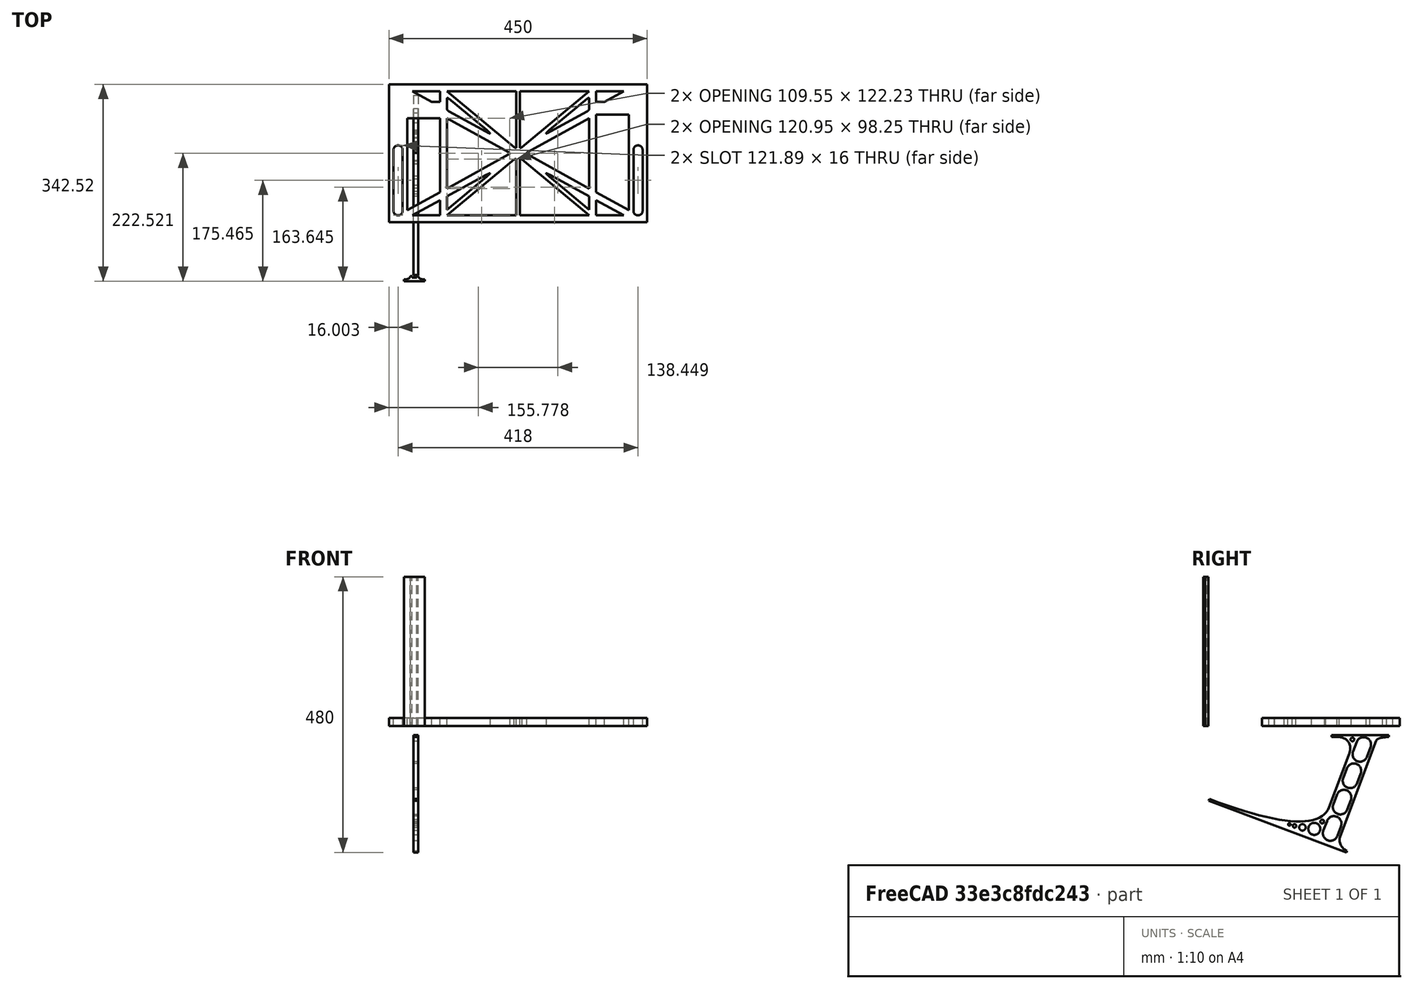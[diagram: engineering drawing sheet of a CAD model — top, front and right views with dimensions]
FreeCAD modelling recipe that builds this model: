
FCSTD DOCUMENT  (FreeCAD 0.19R0.19.2)
Label: laptopStand073
License: All rights reserved
LicenseURL: http://en.wikipedia.org/wiki/All_rights_reserved
objects: Sketcher::SketchObject×3, Part::Extrusion×3
note: 6 computed .brp shape members not serialized (recipe doc carries the construction recipe); baked Part::Feature solids carry a one-line shape summary decoded from their .brp

FEATURE [Sketcher::SketchObject] Sketch
  FullyConstrained = true
  sketch-geometry (148):
    g0: LineSegment StartX=-10.9272 StartY=-82.7794 StartZ=0 EndX=46.0728 EndY=-51.4823 EndZ=0
    g1: LineSegment StartX=366.073 StartY=-91.7794 StartZ=0 EndX=318.073 EndY=-65.424 EndZ=0
    g2: LineSegment StartX=-10.9272 StartY=77.3346 StartZ=0 EndX=-10.9272 EndY=-82.7794 EndZ=0
    g3: LineSegment StartX=375.073 StartY=-82.7794 StartZ=0 EndX=375.073 EndY=83.9235 EndZ=0
    g4: LineSegment StartX=-1.92719 StartY=-91.7794 StartZ=0 EndX=46.0728 EndY=-91.7794 EndZ=0
    g5: LineSegment StartX=318.073 StartY=124.221 StartZ=0 EndX=366.073 EndY=124.221 EndZ=0
    g6: LineSegment StartX=306.073 StartY=124.221 StartZ=0 EndX=189.124 EndY=27.0628 EndZ=0
    g7: LineSegment StartX=58.0728 StartY=-91.7794 StartZ=0 EndX=175.022 EndY=5.37834 EndZ=0
    g8: LineSegment StartX=58.0728 StartY=-81.8102 StartZ=0 EndX=58.0728 EndY=-58.8351 EndZ=0
    g9: LineSegment StartX=175.022 StartY=27.0628 StartZ=0 EndX=58.0728 EndY=124.221 EndZ=0
    g10: LineSegment StartX=189.124 StartY=5.37834 StartZ=0 EndX=306.073 EndY=-91.7794 EndZ=0
    g11: LineSegment StartX=306.073 StartY=77.3346 StartZ=0 EndX=306.073 EndY=-44.8935 EndZ=0
    g12: LineSegment StartX=318.073 StartY=83.9235 StartZ=0 EndX=318.073 EndY=-51.4823 EndZ=0
    g13: LineSegment StartX=306.073 StartY=-58.8351 StartZ=0 EndX=306.073 EndY=-81.8102 EndZ=0
    g14: LineSegment StartX=318.073 StartY=-51.4823 StartZ=0 EndX=375.073 EndY=-82.7794 EndZ=0
    g15: LineSegment StartX=318.073 StartY=-65.424 StartZ=0 EndX=318.073 EndY=-91.7794 EndZ=0
    g16: LineSegment StartX=318.073 StartY=-91.7794 StartZ=0 EndX=366.073 EndY=-91.7794 EndZ=0
    g17: LineSegment StartX=58.0728 StartY=-44.8935 StartZ=0 EndX=58.0728 EndY=77.3346 EndZ=0
    g18: LineSegment StartX=46.0728 StartY=-65.424 StartZ=0 EndX=-1.92719 EndY=-91.7794 EndZ=0
    g19: LineSegment StartX=46.0728 StartY=-65.424 StartZ=0 EndX=46.0728 EndY=-91.7794 EndZ=0
    g20: LineSegment StartX=46.0728 StartY=77.3346 StartZ=0 EndX=46.0728 EndY=-51.4823 EndZ=0
    g21: LineSegment StartX=-42.9272 StartY=136.221 StartZ=0 EndX=-42.9272 EndY=-103.779 EndZ=0
    g22: LineSegment StartX=407.073 StartY=136.221 StartZ=0 EndX=407.073 EndY=-103.779 EndZ=0
    g23: LineSegment StartX=179.022 StartY=27.0628 StartZ=0 EndX=179.022 EndY=124.221 EndZ=0
    g24: LineSegment StartX=185.124 StartY=27.0628 StartZ=0 EndX=185.124 EndY=124.221 EndZ=0
    g25: ArcOfCircle CenterX=-26.9272 CenterY=22.1087 CenterZ=0 NormalX=0 NormalY=0 NormalZ=1 AngleXU=0 Radius=8 StartAngle=1e-16 EndAngle=3.14159
    g26: ArcOfCircle CenterX=-26.9272 CenterY=-83.7794 CenterZ=0 NormalX=0 NormalY=0 NormalZ=1 AngleXU=0 Radius=8 StartAngle=3.14159 EndAngle=6.28319
    g27: LineSegment StartX=-34.9272 StartY=22.1087 StartZ=0 EndX=-34.9272 EndY=-83.7794 EndZ=0
    g28: LineSegment StartX=-18.9272 StartY=22.1087 StartZ=0 EndX=-18.9272 EndY=-83.7794 EndZ=0
    g29: LineSegment StartX=185.124 StartY=-91.7794 StartZ=0 EndX=306.073 EndY=-91.7794 EndZ=0
    g30: LineSegment StartX=179.022 StartY=-91.7794 StartZ=0 EndX=58.0728 EndY=-91.7794 EndZ=0
    g31: LineSegment StartX=306.073 StartY=124.221 StartZ=0 EndX=185.124 EndY=124.221 EndZ=0
    g32: LineSegment StartX=179.022 StartY=124.221 StartZ=0 EndX=58.0728 EndY=124.221 EndZ=0
    g33: ArcOfCircle CenterX=391.073 CenterY=22.1087 CenterZ=0 NormalX=0 NormalY=0 NormalZ=1 AngleXU=0 Radius=8 StartAngle=-4.4e-15 EndAngle=3.14159
    g34: LineSegment StartX=399.073 StartY=22.1087 StartZ=0 EndX=399.073 EndY=-83.7794 EndZ=0
    g35: LineSegment StartX=383.073 StartY=22.1087 StartZ=0 EndX=383.073 EndY=-83.7794 EndZ=0
    g36: ArcOfCircle CenterX=391.073 CenterY=-83.7794 CenterZ=0 NormalX=0 NormalY=0 NormalZ=1 AngleXU=0 Radius=8 StartAngle=3.14159 EndAngle=6.28319
    g37: Circle CenterX=175.022 CenterY=27.0628 CenterZ=0 NormalX=0 NormalY=0 NormalZ=1 AngleXU=0 Radius=1
    g38: Circle CenterX=179.022 CenterY=24.8665 CenterZ=0 NormalX=0 NormalY=0 NormalZ=1 AngleXU=0 Radius=1
    g39: Circle CenterX=179.022 CenterY=27.0628 CenterZ=0 NormalX=0 NormalY=0 NormalZ=1 AngleXU=0 Radius=1
    g40: BSplineCurve PolesCount=3 KnotsCount=2 Degree=2 IsPeriodic=0
    g41: GeomPoint X=175.022 Y=27.0628 Z=0
    g42: GeomPoint X=179.022 Y=27.0628 Z=0
    g43: Circle CenterX=189.124 CenterY=27.0628 CenterZ=0 NormalX=0 NormalY=0 NormalZ=1 AngleXU=0 Radius=1
    g44: Circle CenterX=185.124 CenterY=24.8665 CenterZ=0 NormalX=0 NormalY=0 NormalZ=1 AngleXU=0 Radius=1
    g45: Circle CenterX=185.124 CenterY=27.0628 CenterZ=0 NormalX=0 NormalY=0 NormalZ=1 AngleXU=0 Radius=1
    g46: BSplineCurve PolesCount=3 KnotsCount=2 Degree=2 IsPeriodic=0
    g47: GeomPoint X=189.124 Y=27.0628 Z=0
    g48: GeomPoint X=185.124 Y=27.0628 Z=0
    g49: Circle CenterX=175.022 CenterY=5.37834 CenterZ=0 NormalX=0 NormalY=0 NormalZ=1 AngleXU=0 Radius=1
    g50: Circle CenterX=179.022 CenterY=7.57463 CenterZ=0 NormalX=0 NormalY=0 NormalZ=1 AngleXU=0 Radius=1
    g51: Circle CenterX=179.022 CenterY=5.34704 CenterZ=0 NormalX=0 NormalY=0 NormalZ=1 AngleXU=0 Radius=1
    g52: BSplineCurve PolesCount=3 KnotsCount=2 Degree=2 IsPeriodic=0
    g53: GeomPoint X=175.022 Y=5.37834 Z=0
    g54: GeomPoint X=179.022 Y=5.34704 Z=0
    g55: Circle CenterX=189.124 CenterY=5.37834 CenterZ=0 NormalX=0 NormalY=0 NormalZ=1 AngleXU=0 Radius=1
    g56: Circle CenterX=185.124 CenterY=7.57463 CenterZ=0 NormalX=0 NormalY=0 NormalZ=1 AngleXU=0 Radius=1
    g57: Circle CenterX=185.124 CenterY=5.34704 CenterZ=0 NormalX=0 NormalY=0 NormalZ=1 AngleXU=0 Radius=1
    g58: BSplineCurve PolesCount=3 KnotsCount=2 Degree=2 IsPeriodic=0
    g59: GeomPoint X=189.124 Y=5.37834 Z=0
    g60: GeomPoint X=185.124 Y=5.34704 Z=0
    g61: LineSegment StartX=179.022 StartY=5.34704 StartZ=0 EndX=179.022 EndY=-91.7794 EndZ=0
    g62: LineSegment StartX=185.124 StartY=-91.7794 StartZ=0 EndX=185.124 EndY=5.34704 EndZ=0
    g63: Circle CenterX=165.871 CenterY=18.1458 CenterZ=0 NormalX=0 NormalY=0 NormalZ=1 AngleXU=0 Radius=1
    g64: Circle CenterX=169.377 CenterY=16.2206 CenterZ=0 NormalX=0 NormalY=0 NormalZ=1 AngleXU=0 Radius=1
    g65: Circle CenterX=165.871 CenterY=14.2954 CenterZ=0 NormalX=0 NormalY=0 NormalZ=1 AngleXU=0 Radius=1
    g66: BSplineCurve PolesCount=3 KnotsCount=2 Degree=2 IsPeriodic=0
    g67: GeomPoint X=165.871 Y=18.1458 Z=0
    g68: GeomPoint X=165.871 Y=14.2954 Z=0
    g69: Circle CenterX=198.275 CenterY=18.1458 CenterZ=0 NormalX=0 NormalY=0 NormalZ=1 AngleXU=0 Radius=1
    g70: Circle CenterX=194.768 CenterY=16.2206 CenterZ=0 NormalX=0 NormalY=0 NormalZ=1 AngleXU=0 Radius=1
    g71: Circle CenterX=198.275 CenterY=14.2954 CenterZ=0 NormalX=0 NormalY=0 NormalZ=1 AngleXU=0 Radius=1
    g72: BSplineCurve PolesCount=3 KnotsCount=2 Degree=2 IsPeriodic=0
    g73: GeomPoint X=198.275 Y=18.1458 Z=0
    g74: GeomPoint X=198.275 Y=14.2954 Z=0
    g75: LineSegment StartX=165.871 StartY=18.1458 StartZ=0 EndX=58.0728 EndY=77.3346 EndZ=0
    g76: LineSegment StartX=58.0728 StartY=-44.8935 StartZ=0 EndX=165.871 EndY=14.2954 EndZ=0
    g77: LineSegment StartX=198.275 StartY=18.1458 StartZ=0 EndX=306.073 EndY=77.3346 EndZ=0
    g78: LineSegment StartX=198.275 StartY=14.2954 StartZ=0 EndX=306.073 EndY=-44.8935 EndZ=0
    g79: LineSegment StartX=407.073 StartY=-103.779 StartZ=0 EndX=-42.9272 EndY=-103.779 EndZ=0
    g80: LineSegment StartX=407.073 StartY=136.221 StartZ=0 EndX=-42.9272 EndY=136.221 EndZ=0
    g81: LineSegment StartX=46.0728 StartY=77.3346 StartZ=0 EndX=-10.9272 EndY=77.3346 EndZ=0
    g82: LineSegment StartX=46.0728 StartY=105.865 StartZ=0 EndX=31.5028 EndY=105.865 EndZ=0
    g83: LineSegment StartX=46.0728 StartY=124.221 StartZ=0 EndX=46.0728 EndY=105.865 EndZ=0
    g84: LineSegment StartX=-1.92719 StartY=124.221 StartZ=0 EndX=31.5028 EndY=105.865 EndZ=0
    g85: LineSegment StartX=46.0728 StartY=124.221 StartZ=0 EndX=-1.92719 EndY=124.221 EndZ=0
    g86: LineSegment StartX=318.073 StartY=83.9235 StartZ=0 EndX=375.073 EndY=83.9235 EndZ=0
    g87: LineSegment StartX=318.073 StartY=105.865 StartZ=0 EndX=332.643 EndY=105.865 EndZ=0
    g88: LineSegment StartX=332.643 StartY=105.865 StartZ=0 EndX=366.073 EndY=124.221 EndZ=0
    g89: LineSegment StartX=318.073 StartY=124.221 StartZ=0 EndX=318.073 EndY=105.865 EndZ=0
    g90: Circle CenterX=125.607 CenterY=54.1951 CenterZ=0 NormalX=0 NormalY=0 NormalZ=1 AngleXU=0 Radius=1
    g91: Circle CenterX=139.632 CenterY=46.4944 CenterZ=0 NormalX=0 NormalY=0 NormalZ=1 AngleXU=0 Radius=1
    g92: Circle CenterX=127.326 CenterY=56.7187 CenterZ=0 NormalX=0 NormalY=0 NormalZ=1 AngleXU=0 Radius=1
    g93: BSplineCurve PolesCount=3 KnotsCount=2 Degree=2 IsPeriodic=0
    g94: GeomPoint X=125.607 Y=54.1951 Z=0
    g95: GeomPoint X=127.326 Y=56.7187 Z=0
    g96: Circle CenterX=236.821 CenterY=56.7187 CenterZ=0 NormalX=0 NormalY=0 NormalZ=1 AngleXU=0 Radius=1
    g97: Circle CenterX=224.513 CenterY=46.4944 CenterZ=0 NormalX=0 NormalY=0 NormalZ=1 AngleXU=0 Radius=1
    g98: Circle CenterX=238.538 CenterY=54.1951 CenterZ=0 NormalX=0 NormalY=0 NormalZ=1 AngleXU=0 Radius=1
    g99: BSplineCurve PolesCount=3 KnotsCount=2 Degree=2 IsPeriodic=0
    g100: GeomPoint X=236.821 Y=56.7187 Z=0
    g101: GeomPoint X=238.538 Y=54.1951 Z=0
    g102: Circle CenterX=238.538 CenterY=-21.7539 CenterZ=0 NormalX=0 NormalY=0 NormalZ=1 AngleXU=0 Radius=1
    g103: Circle CenterX=224.513 CenterY=-14.0532 CenterZ=0 NormalX=0 NormalY=0 NormalZ=1 AngleXU=0 Radius=1
    g104: Circle CenterX=236.821 CenterY=-24.2775 CenterZ=0 NormalX=0 NormalY=0 NormalZ=1 AngleXU=0 Radius=1
    g105: BSplineCurve PolesCount=3 KnotsCount=2 Degree=2 IsPeriodic=0
    g106: GeomPoint X=238.538 Y=-21.7539 Z=0
    g107: GeomPoint X=236.821 Y=-24.2775 Z=0
    g108: LineSegment StartX=238.538 StartY=-21.7539 StartZ=0 EndX=306.073 EndY=-58.8351 EndZ=0
    g109: LineSegment StartX=236.821 StartY=-24.2775 StartZ=0 EndX=306.073 EndY=-81.8102 EndZ=0
    g110: Circle CenterX=125.607 CenterY=-21.7539 CenterZ=0 NormalX=0 NormalY=0 NormalZ=1 AngleXU=0 Radius=1
    g111: Circle CenterX=139.632 CenterY=-14.0532 CenterZ=0 NormalX=0 NormalY=0 NormalZ=1 AngleXU=0 Radius=1
    g112: Circle CenterX=127.325 CenterY=-24.2775 CenterZ=0 NormalX=0 NormalY=0 NormalZ=1 AngleXU=0 Radius=1
    g113: BSplineCurve PolesCount=3 KnotsCount=2 Degree=2 IsPeriodic=0
    g114: GeomPoint X=125.607 Y=-21.7539 Z=0
    g115: GeomPoint X=127.325 Y=-24.2775 Z=0
    g116: LineSegment StartX=125.607 StartY=-21.7539 StartZ=0 EndX=58.0728 EndY=-58.8351 EndZ=0
    g117: LineSegment StartX=127.325 StartY=-24.2775 StartZ=0 EndX=58.0728 EndY=-81.8102 EndZ=0
    g118: Circle CenterX=302.996 CenterY=111.695 CenterZ=0 NormalX=0 NormalY=0 NormalZ=1 AngleXU=0 Radius=1
    g119: Circle CenterX=306.073 CenterY=114.251 CenterZ=0 NormalX=0 NormalY=0 NormalZ=1 AngleXU=0 Radius=1
    g120: Circle CenterX=306.073 CenterY=110.251 CenterZ=0 NormalX=0 NormalY=0 NormalZ=1 AngleXU=0 Radius=1
    g121: BSplineCurve PolesCount=3 KnotsCount=2 Degree=2 IsPeriodic=0
    g122: GeomPoint X=302.996 Y=111.695 Z=0
    g123: GeomPoint X=306.073 Y=110.251 Z=0
    g124: Circle CenterX=306.073 CenterY=95.2763 CenterZ=0 NormalX=0 NormalY=0 NormalZ=1 AngleXU=0 Radius=1
    g125: Circle CenterX=306.073 CenterY=91.2763 CenterZ=0 NormalX=0 NormalY=0 NormalZ=1 AngleXU=0 Radius=1
    g126: Circle CenterX=302.567 CenterY=89.3511 CenterZ=0 NormalX=0 NormalY=0 NormalZ=1 AngleXU=0 Radius=1
    g127: BSplineCurve PolesCount=3 KnotsCount=2 Degree=2 IsPeriodic=0
    g128: GeomPoint X=306.073 Y=95.2763 Z=0
    g129: GeomPoint X=302.567 Y=89.3511 Z=0
    g130: LineSegment StartX=306.073 StartY=110.251 StartZ=0 EndX=306.073 EndY=95.2763 EndZ=0
    g131: LineSegment StartX=302.996 StartY=111.695 StartZ=0 EndX=236.821 EndY=56.7187 EndZ=0
    g132: LineSegment StartX=238.538 StartY=54.1951 StartZ=0 EndX=302.567 EndY=89.3511 EndZ=0
    g133: Circle CenterX=61.1496 CenterY=111.695 CenterZ=0 NormalX=0 NormalY=0 NormalZ=1 AngleXU=0 Radius=1
    g134: Circle CenterX=58.0728 CenterY=114.251 CenterZ=0 NormalX=0 NormalY=0 NormalZ=1 AngleXU=0 Radius=1
    g135: Circle CenterX=58.0728 CenterY=110.251 CenterZ=0 NormalX=0 NormalY=0 NormalZ=1 AngleXU=0 Radius=1
    g136: BSplineCurve PolesCount=3 KnotsCount=2 Degree=2 IsPeriodic=0
    g137: GeomPoint X=61.1496 Y=111.695 Z=0
    g138: GeomPoint X=58.0728 Y=110.251 Z=0
    g139: Circle CenterX=61.5791 CenterY=89.3511 CenterZ=0 NormalX=0 NormalY=0 NormalZ=1 AngleXU=0 Radius=1
    g140: Circle CenterX=58.0728 CenterY=91.2763 CenterZ=0 NormalX=0 NormalY=0 NormalZ=1 AngleXU=0 Radius=1
    g141: Circle CenterX=58.0728 CenterY=95.2763 CenterZ=0 NormalX=0 NormalY=0 NormalZ=1 AngleXU=0 Radius=1
    g142: BSplineCurve PolesCount=3 KnotsCount=2 Degree=2 IsPeriodic=0
    g143: GeomPoint X=61.5791 Y=89.3511 Z=0
    g144: GeomPoint X=58.0728 Y=95.2763 Z=0
    g145: LineSegment StartX=58.0728 StartY=110.251 StartZ=0 EndX=58.0728 EndY=95.2763 EndZ=0
    g146: LineSegment StartX=61.1496 StartY=111.695 StartZ=0 EndX=127.326 EndY=56.7187 EndZ=0
    g147: LineSegment StartX=125.607 StartY=54.1951 StartZ=0 EndX=61.5791 EndY=89.3511 EndZ=0
  constraints (262):
    c: Horizontal(g4)
    c: Horizontal(g5)
    c: Tangent(g11,g13)
    c: Coincident(g12,g14)
    c: Coincident(g15,g1)
    c: Tangent(g12,g15)
    c: Tangent(g8,g17)
    c: Coincident(g19,g18)
    c: Coincident(g0,g20)
    c: Block(g9)
    c: Block(g6)
    c: Block(g14)
    c: Block(g3)
    c: Block(g13)
    c: Block(g1)
    c: Block(g15)
    c: Block(g10)
    c: Block(g7)
    c: Block(g19)
    c: Block(g18)
    c: Block(g0)
    c: Block(g2)
    c: Block(g11)
    c: Block(g5)
    c: Block(g16)
    c: Block(g4)
    c: Vertical(g21)
    c: Vertical(g22)
    c: Block(g22)
    c: Block(g21)
    c: Vertical(g23)
    c: Vertical(g24)
    c: Block(g23)
    c: Block(g24)
    c: Tangent(g25,g28) = 1.5708
    c: Tangent(g25,g27) = -1.5708
    c: Tangent(g27,g26) = -1.5708
    c: Tangent(g28,g26) = 1.5708
    c: Vertical(g27)
    c: Equal(g25,g26)
    c: Block(g28)
    c: Block(g27)
    c: Coincident(g29,g10)
    c: Horizontal(g29)
    c: Coincident(g30,g7)
    c: Horizontal(g30)
    c: Coincident(g31,g6)
    c: Coincident(g31,g24)
    c: Horizontal(g31)
    c: Coincident(g32,g23)
    c: Coincident(g32,g9)
    c: Horizontal(g32)
    c: Tangent(g33,g34) = 1.5708
    c: Tangent(g34,g36) = 1.5708
    c: Equal(g33,g36)
    c: Coincident(g35,g33)
    c: Coincident(g35,g36)
    c: Block(g34)
    c: Block(g35)
    c: Coincident(g40,g9)
    c: Weight(g37) = 1
    c: Equal(g37,g38)
    c: Equal(g37,g39)
    c: Coincident(g40,g23)
    c: InternalAlignment(g37,g40)
    c: InternalAlignment(g38,g40)
    c: InternalAlignment(g39,g40)
    c: InternalAlignment(g41,g40)
    c: InternalAlignment(g42,g40)
    c: Coincident(g46,g6)
    c: Weight(g43) = 1
    c: Equal(g43,g44)
    c: Equal(g43,g45)
    c: Coincident(g46,g24)
    c: InternalAlignment(g43,g46)
    c: InternalAlignment(g44,g46)
    c: InternalAlignment(g45,g46)
    c: InternalAlignment(g47,g46)
    c: InternalAlignment(g48,g46)
    c: Block(g46)
    c: Block(g40)
    c: Coincident(g52,g7)
    c: Weight(g49) = 1
    c: Equal(g49,g50)
    c: Equal(g49,g51)
    c: InternalAlignment(g49,g52)
    c: InternalAlignment(g50,g52)
    c: InternalAlignment(g51,g52)
    c: InternalAlignment(g53,g52)
    c: InternalAlignment(g54,g52)
    c: Weight(g55) = 1
    c: Equal(g55,g56)
    c: Equal(g55,g57)
    c: InternalAlignment(g55,g58)
    c: InternalAlignment(g56,g58)
    c: InternalAlignment(g57,g58)
    c: InternalAlignment(g59,g58)
    c: InternalAlignment(g60,g58)
    c: Block(g58)
    c: Block(g52)
    c: Coincident(g61,g52)
    c: Coincident(g61,g30)
    c: Vertical(g61)
    c: Coincident(g62,g29)
    c: Coincident(g62,g58)
    c: Vertical(g62)
    c: Weight(g63) = 1
    c: Equal(g63,g64)
    c: Equal(g63,g65)
    c: InternalAlignment(g63,g66)
    c: InternalAlignment(g64,g66)
    c: InternalAlignment(g65,g66)
    c: InternalAlignment(g67,g66)
    c: InternalAlignment(g68,g66)
    c: Weight(g69) = 1
    c: Equal(g69,g70)
    c: Equal(g69,g71)
    c: InternalAlignment(g69,g72)
    c: InternalAlignment(g70,g72)
    c: InternalAlignment(g71,g72)
    c: InternalAlignment(g73,g72)
    c: InternalAlignment(g74,g72)
    c: Block(g66)
    c: Block(g72)
    c: Coincident(g75,g66)
    c: Coincident(g75,g17)
    c: Coincident(g76,g17)
    c: Coincident(g76,g66)
    c: Coincident(g77,g72)
    c: Coincident(g77,g11)
    c: Coincident(g78,g72)
    c: Coincident(g78,g11)
    c: Block(g17)
    c: Coincident(g79,g22)
    c: Coincident(g79,g21)
    c: Horizontal(g79)
    c: Distance(g79) = 450
    c: Coincident(g80,g22)
    c: Coincident(g80,g21)
    c: Horizontal(g80)
    c: Horizontal(g81)
    c: Coincident(g20,g81)
    c: Horizontal(g82)
    c: Vertical(g83)
    c: Block(g83)
    c: Block(g82)
    c: Block(g81)
    c: Distance(g83) = 18.3554
    c: Coincident(g85,g83)
    c: Coincident(g85,g84)
    c: Horizontal(g85)
    c: Block(g85)
    c: Block(g84)
    c: Coincident(g82,g84)
    c: Coincident(g2,g81)
    c: Coincident(g86,g12)
    c: Horizontal(g86)
    c: Horizontal(g87)
    c: Block(g86)
    c: Coincident(g88,g5)
    c: Coincident(g89,g5)
    c: Coincident(g89,g87)
    c: Vertical(g89)
    c: Block(g89)
    c: Coincident(g87,g88)
    c: Block(g88)
    c: Coincident(g3,g86)
    c: Weight(g90) = 1
    c: Equal(g90,g91)
    c: Equal(g90,g92)
    c: InternalAlignment(g90,g93)
    c: InternalAlignment(g91,g93)
    c: InternalAlignment(g92,g93)
    c: InternalAlignment(g94,g93)
    c: InternalAlignment(g95,g93)
    c: Block(g93)
    c: Weight(g96) = 1
    c: Equal(g96,g97)
    c: Equal(g96,g98)
    c: InternalAlignment(g96,g99)
    c: InternalAlignment(g97,g99)
    c: InternalAlignment(g98,g99)
    c: InternalAlignment(g100,g99)
    c: InternalAlignment(g101,g99)
    c: Block(g99)
    c: Weight(g102) = 1
    c: Equal(g102,g103)
    c: Equal(g102,g104)
    c: InternalAlignment(g102,g105)
    c: InternalAlignment(g103,g105)
    c: InternalAlignment(g104,g105)
    c: InternalAlignment(g106,g105)
    c: InternalAlignment(g107,g105)
    c: Block(g105)
    c: Coincident(g108,g105)
    c: Coincident(g108,g13)
    c: Coincident(g109,g105)
    c: Coincident(g109,g13)
    c: Weight(g110) = 1
    c: Equal(g110,g111)
    c: Equal(g110,g112)
    c: InternalAlignment(g110,g113)
    c: InternalAlignment(g111,g113)
    c: InternalAlignment(g112,g113)
    c: InternalAlignment(g114,g113)
    c: InternalAlignment(g115,g113)
    c: Block(g113)
    c: Coincident(g116,g113)
    c: Coincident(g116,g8)
    c: Coincident(g117,g113)
    c: Coincident(g117,g8)
    c: Block(g8)
    c: Weight(g118) = 1
    c: Equal(g118,g119)
    c: Equal(g118,g120)
    c: InternalAlignment(g118,g121)
    c: InternalAlignment(g119,g121)
    c: InternalAlignment(g120,g121)
    c: InternalAlignment(g122,g121)
    c: InternalAlignment(g123,g121)
    c: Weight(g124) = 1
    c: Equal(g124,g125)
    c: Equal(g124,g126)
    c: InternalAlignment(g124,g127)
    c: InternalAlignment(g125,g127)
    c: InternalAlignment(g126,g127)
    c: InternalAlignment(g128,g127)
    c: InternalAlignment(g129,g127)
    c: Block(g121)
    c: Block(g127)
    c: Coincident(g130,g121)
    c: Coincident(g130,g127)
    c: Vertical(g130)
    c: Coincident(g131,g121)
    c: Coincident(g131,g99)
    c: Coincident(g132,g99)
    c: Coincident(g132,g127)
    c: Weight(g133) = 1
    c: Equal(g133,g134)
    c: Equal(g133,g135)
    c: InternalAlignment(g133,g136)
    c: InternalAlignment(g134,g136)
    c: InternalAlignment(g135,g136)
    c: InternalAlignment(g137,g136)
    c: InternalAlignment(g138,g136)
    c: Weight(g139) = 1
    c: Equal(g139,g140)
    c: Equal(g139,g141)
    c: InternalAlignment(g139,g142)
    c: InternalAlignment(g140,g142)
    c: InternalAlignment(g141,g142)
    c: InternalAlignment(g143,g142)
    c: InternalAlignment(g144,g142)
    c: Block(g136)
    c: Block(g142)
    c: Coincident(g145,g136)
    c: Coincident(g145,g142)
    c: Vertical(g145)
    c: Coincident(g146,g136)
    c: Coincident(g146,g93)
    c: Coincident(g147,g93)
    c: Coincident(g147,g142)
FEATURE [Sketcher::SketchObject] Sketch001
  FullyConstrained = true
  MapMode = 4
  Placement = pos=(0,0,0) rot=(0.57735,0.57735,0.57735;2.0944rad)
  Support = -> [Sketch]
  sketch-geometry (46):
    g0: BSplineCurve PolesCount=3 KnotsCount=2 Degree=2 IsPeriodic=0
    g1: ArcOfCircle CenterX=73.1223 CenterY=-32.291 CenterZ=0 NormalX=0 NormalY=0 NormalZ=1 AngleXU=0 Radius=13 StartAngle=5.92268 EndAngle=9.06428
    g2: ArcOfCircle CenterX=66.7816 CenterY=-49.1439 CenterZ=0 NormalX=0 NormalY=0 NormalZ=1 AngleXU=0 Radius=13 StartAngle=2.78068 EndAngle=5.92131
    g3: ArcOfCircle CenterX=55.9263 CenterY=-78.1807 CenterZ=0 NormalX=0 NormalY=0 NormalZ=1 AngleXU=0 Radius=13 StartAngle=5.92268 EndAngle=9.06428
    g4: ArcOfCircle CenterX=49.5884 CenterY=-95.0342 CenterZ=0 NormalX=0 NormalY=0 NormalZ=1 AngleXU=0 Radius=13 StartAngle=2.78068 EndAngle=5.92131
    g5: ArcOfCircle CenterX=38.7206 CenterY=-124.067 CenterZ=0 NormalX=0 NormalY=0 NormalZ=1 AngleXU=0 Radius=13 StartAngle=5.92268 EndAngle=9.06428
    g6: ArcOfCircle CenterX=32.3875 CenterY=-140.92 CenterZ=0 NormalX=0 NormalY=0 NormalZ=1 AngleXU=0 Radius=13 StartAngle=2.78068 EndAngle=5.92131
    g7: ArcOfCircle CenterX=21.4715 CenterY=-169.934 CenterZ=0 NormalX=0 NormalY=0 NormalZ=1 AngleXU=0 Radius=13 StartAngle=5.92268 EndAngle=9.06428
    g8: ArcOfCircle CenterX=15.1336 CenterY=-186.787 CenterZ=0 NormalX=0 NormalY=0 NormalZ=1 AngleXU=0 Radius=13 StartAngle=2.78068 EndAngle=5.92131
    g9-g12: Circle x4 (B-spline internal-alignment scaffolding for g13; pole/knot coordinates omitted)
    g13: BSplineCurve PolesCount=4 KnotsCount=2 Degree=3 IsPeriodic=0
    g14: GeomPoint X=28.8094 Y=-19.0875 Z=0
    g15: GeomPoint X=47.0443 Y=-50.4712 Z=0
    g16: Circle CenterX=53.5586 CenterY=-23.2695 CenterZ=0 NormalX=0 NormalY=0 NormalZ=1 AngleXU=0 Radius=3.24518
    g17: Circle CenterX=-195.441 CenterY=-127.082 CenterZ=0 NormalX=0 NormalY=0 NormalZ=1 AngleXU=0 Radius=1
    g18: Circle CenterX=-8.24091 CenterY=-197.481 CenterZ=0 NormalX=0 NormalY=0 NormalZ=1 AngleXU=0 Radius=1
    g19: Circle CenterX=12.8789 CenterY=-141.321 CenterZ=0 NormalX=0 NormalY=0 NormalZ=1 AngleXU=0 Radius=1
    g20: BSplineCurve PolesCount=3 KnotsCount=2 Degree=2 IsPeriodic=0
    g21: GeomPoint X=-195.441 Y=-127.082 Z=0
    g22: GeomPoint X=12.8789 Y=-141.321 Z=0
    g23: Circle CenterX=-12.8016 CenterY=-179.036 CenterZ=0 NormalX=0 NormalY=0 NormalZ=1 AngleXU=0 Radius=10.5072
    g24: Circle CenterX=0.933922 CenterY=-166.43 CenterZ=0 NormalX=0 NormalY=0 NormalZ=1 AngleXU=0 Radius=3.26661
    g25: Circle CenterX=-33.5518 CenterY=-176.44 CenterZ=0 NormalX=0 NormalY=0 NormalZ=1 AngleXU=0 Radius=5.64388
    g26: Circle CenterX=-47.2366 CenterY=-173.859 CenterZ=0 NormalX=0 NormalY=0 NormalZ=1 AngleXU=0 Radius=3.01653
    g27: Circle CenterX=-56.2595 CenterY=-171.456 CenterZ=0 NormalX=0 NormalY=0 NormalZ=1 AngleXU=0 Radius=2.12826
    g28: ArcOfCircle CenterX=51.2151 CenterY=-198.473 CenterZ=0 NormalX=0 NormalY=0 NormalZ=1 AngleXU=0 Radius=20 StartAngle=2.78189 EndAngle=4.35269
    g29: LineSegment StartX=32.4951 StartY=-191.433 StartZ=0 EndX=94.6578 EndY=-26.1352 EndZ=0
    g30: LineSegment StartX=43.1192 StartY=-220.001 StartZ=0 EndX=-196.497 EndY=-129.89 EndZ=0
    g31: LineSegment StartX=43.1192 StartY=-220.001 StartZ=0 EndX=44.1752 EndY=-217.193 EndZ=0
    g32: LineSegment StartX=117.223 StartY=-19.0875 StartZ=0 EndX=117.223 EndY=-16.0875 EndZ=0
    g33: LineSegment StartX=117.223 StartY=-16.0875 StartZ=0 EndX=17.2232 EndY=-16.0875 EndZ=0
    g34: LineSegment StartX=17.2232 StartY=-16.0875 StartZ=0 EndX=17.2232 EndY=-19.0875 EndZ=0
    g35: LineSegment StartX=28.8094 StartY=-19.0875 StartZ=0 EndX=17.2232 EndY=-19.0875 EndZ=0
    g36: LineSegment StartX=47.0443 StartY=-50.4712 StartZ=0 EndX=12.8789 EndY=-141.321 EndZ=0
    g37: LineSegment StartX=-195.441 StartY=-127.082 StartZ=0 EndX=-196.497 EndY=-129.89 EndZ=0
    g38: LineSegment StartX=85.2866 StartY=-36.8766 StartZ=0 EndX=78.9396 EndY=-53.7463 EndZ=0
    g39: LineSegment StartX=60.9579 StartY=-27.7053 StartZ=0 EndX=54.6191 EndY=-44.5532 EndZ=0
    g40: LineSegment StartX=68.0907 StartY=-82.7664 StartZ=0 EndX=61.7465 EndY=-99.6365 EndZ=0
    g41: LineSegment StartX=43.7619 StartY=-73.595 StartZ=0 EndX=37.426 EndY=-90.4435 EndZ=0
    g42: LineSegment StartX=50.885 StartY=-128.652 StartZ=0 EndX=44.5456 EndY=-145.522 EndZ=0
    g43: LineSegment StartX=26.5562 StartY=-119.481 StartZ=0 EndX=20.2251 EndY=-136.329 EndZ=0
    g44: LineSegment StartX=9.3071 StartY=-165.349 StartZ=0 EndX=2.97115 EndY=-182.197 EndZ=0
    g45: LineSegment StartX=33.6358 StartY=-174.52 StartZ=0 EndX=27.2917 EndY=-191.39 EndZ=0
  constraints (71):
    c: Block(g0)
    c: Block(g1)
    c: Block(g2)
    c: Block(g4)
    c: Block(g3)
    c: Block(g6)
    c: Block(g5)
    c: Block(g8)
    c: Block(g7)
    c: Weight(g9) = 1
    c: Equal(g9,g10)
    c: Equal(g9,g11)
    c: Equal(g9,g12)
    c: InternalAlignment(g9-g12 -> g13) x4
    c: InternalAlignment(g14,g13)
    c: InternalAlignment(g15,g13)
    c: Block(g16)
    c: Weight(g17) = 1
    c: Equal(g17,g18)
    c: Equal(g17,g19)
    c: InternalAlignment(g17,g20)
    c: InternalAlignment(g18,g20)
    c: InternalAlignment(g19,g20)
    c: InternalAlignment(g21,g20)
    c: InternalAlignment(g22,g20)
    c: Block(g20)
    c: Block(g23)
    c: Block(g24)
    c: Block(g25)
    c: Block(g26)
    c: Block(g27)
    c: Block(g28)
    c: Coincident(g29,g28)
    c: Coincident(g29,g0)
    c: Block(g13)
    c: Coincident(g31,g30)
    c: Coincident(g31,g28)
    c: Block(g31)
    c: Coincident(g32,g0)
    c: Vertical(g32)
    c: Coincident(g33,g32)
    c: Horizontal(g33)
    c: Coincident(g34,g33)
    c: Vertical(g34)
    c: Block(g33)
    c: Coincident(g35,g13)
    c: Coincident(g35,g34)
    c: Horizontal(g35)
    c: Coincident(g36,g13)
    c: Coincident(g36,g20)
    c: Coincident(g37,g20)
    c: Coincident(g37,g30)
    c: Block(g30)
    c: Coincident(g38,g1)
    c: Coincident(g38,g2)
    c: Coincident(g39,g1)
    c: Coincident(g39,g2)
    c: Coincident(g40,g3)
    c: Coincident(g40,g4)
    c: Coincident(g41,g3)
    c: Coincident(g41,g4)
    c: Coincident(g42,g5)
    c: Coincident(g42,g6)
    c: Coincident(g43,g5)
    c: Coincident(g43,g6)
    c: Coincident(g44,g7)
    c: Coincident(g44,g8)
    c: Coincident(g45,g7)
    c: Coincident(g45,g8)
    c: Distance(g30) = 256
    c: Distance(g33) = 100
FEATURE [Part::Extrusion] Extrude002
  Base = -> Sketch001
  Dir = (1,0,0)
  DirMode = 2
  FaceMakerClass = Part::FaceMakerBullseye
  LengthFwd = 8
  LengthRev = 0
  Solid = true
  Symmetric = false
FEATURE [Sketcher::SketchObject] Sketch002
  FullyConstrained = true
  sketch-geometry (20):
    g0: LineSegment StartX=-2.77179 StartY=-200.304 StartZ=0 EndX=5.22821 EndY=-200.304 EndZ=0
    g1: LineSegment StartX=5.22821 StartY=-200.304 StartZ=0 EndX=5.22821 EndY=-197.304 EndZ=0
    g2: LineSegment StartX=-2.77179 StartY=-200.304 StartZ=0 EndX=-2.77179 EndY=-197.304 EndZ=0
    g3: LineSegment StartX=5.22821 StartY=-197.304 StartZ=0 EndX=8.22821 EndY=-197.304 EndZ=0
    g4: LineSegment StartX=-2.77179 StartY=-197.304 StartZ=0 EndX=-5.77179 EndY=-197.304 EndZ=0
    g5: LineSegment StartX=19.2282 StartY=-203.304 StartZ=0 EndX=19.2282 EndY=-206.304 EndZ=0
    g6: LineSegment StartX=-16.7718 StartY=-203.304 StartZ=0 EndX=-16.7718 EndY=-206.304 EndZ=0
    g7: LineSegment StartX=-16.7718 StartY=-206.304 StartZ=0 EndX=19.2282 EndY=-206.304 EndZ=0
    g8: Circle CenterX=-16.7718 CenterY=-203.304 CenterZ=0 NormalX=0 NormalY=0 NormalZ=1 AngleXU=0 Radius=1
    g9: Circle CenterX=-5.77179 CenterY=-203.304 CenterZ=0 NormalX=0 NormalY=0 NormalZ=1 AngleXU=0 Radius=1
    g10: Circle CenterX=-5.77179 CenterY=-197.304 CenterZ=0 NormalX=0 NormalY=0 NormalZ=1 AngleXU=0 Radius=1
    g11: BSplineCurve PolesCount=3 KnotsCount=2 Degree=2 IsPeriodic=0
    g12: GeomPoint X=-16.7718 Y=-203.304 Z=0
    g13: GeomPoint X=-5.77179 Y=-197.304 Z=0
    g14: Circle CenterX=19.2282 CenterY=-203.304 CenterZ=0 NormalX=0 NormalY=0 NormalZ=1 AngleXU=0 Radius=1
    g15: Circle CenterX=8.22821 CenterY=-203.304 CenterZ=0 NormalX=0 NormalY=0 NormalZ=1 AngleXU=0 Radius=1
    g16: Circle CenterX=8.22821 CenterY=-197.304 CenterZ=0 NormalX=0 NormalY=0 NormalZ=1 AngleXU=0 Radius=1
    g17: BSplineCurve PolesCount=3 KnotsCount=2 Degree=2 IsPeriodic=0
    g18: GeomPoint X=19.2282 Y=-203.304 Z=0
    g19: GeomPoint X=8.22821 Y=-197.304 Z=0
  constraints (41):
    c: Horizontal(g0)
    c: Distance(g0) = 8
    c: Coincident(g1,g0)
    c: Vertical(g1)
    c: Distance(g1) = 3
    c: Coincident(g2,g0)
    c: Vertical(g2)
    c: Distance(g2) = 3
    c: Coincident(g3,g1)
    c: Horizontal(g3)
    c: Distance(g3) = 3
    c: Coincident(g4,g2)
    c: Horizontal(g4)
    c: Distance(g4) = 3
    c: Vertical(g5)
    c: Vertical(g6)
    c: Coincident(g7,g6)
    c: Coincident(g7,g5)
    c: Weight(g8) = 1
    c: Equal(g8,g9)
    c: Equal(g8,g10)
    c: Coincident(g11,g4)
    c: InternalAlignment(g8,g11)
    c: InternalAlignment(g9,g11)
    c: InternalAlignment(g10,g11)
    c: InternalAlignment(g12,g11)
    c: InternalAlignment(g13,g11)
    c: Coincident(g17,g5)
    c: Weight(g14) = 1
    c: Equal(g14,g15)
    c: Equal(g14,g16)
    c: Coincident(g17,g3)
    c: InternalAlignment(g14,g17)
    c: InternalAlignment(g15,g17)
    c: InternalAlignment(g16,g17)
    c: InternalAlignment(g18,g17)
    c: InternalAlignment(g19,g17)
    c: Block(g7)
    c: Block(g17)
    c: Block(g11)
    c: Block(g6)
FEATURE [Part::Extrusion] Extrude003
  Base = -> Sketch002
  Dir = (0,0,1)
  DirMode = 2
  FaceMakerClass = Part::FaceMakerBullseye
  LengthFwd = 260
  LengthRev = 0
  Solid = true
  Symmetric = false
FEATURE [Part::Extrusion] Extrude
  Base = -> Sketch
  Dir = (0,0,1)
  DirMode = 2
  FaceMakerClass = Part::FaceMakerBullseye
  LengthFwd = 14
  LengthRev = 0
  Solid = true
  Symmetric = false
